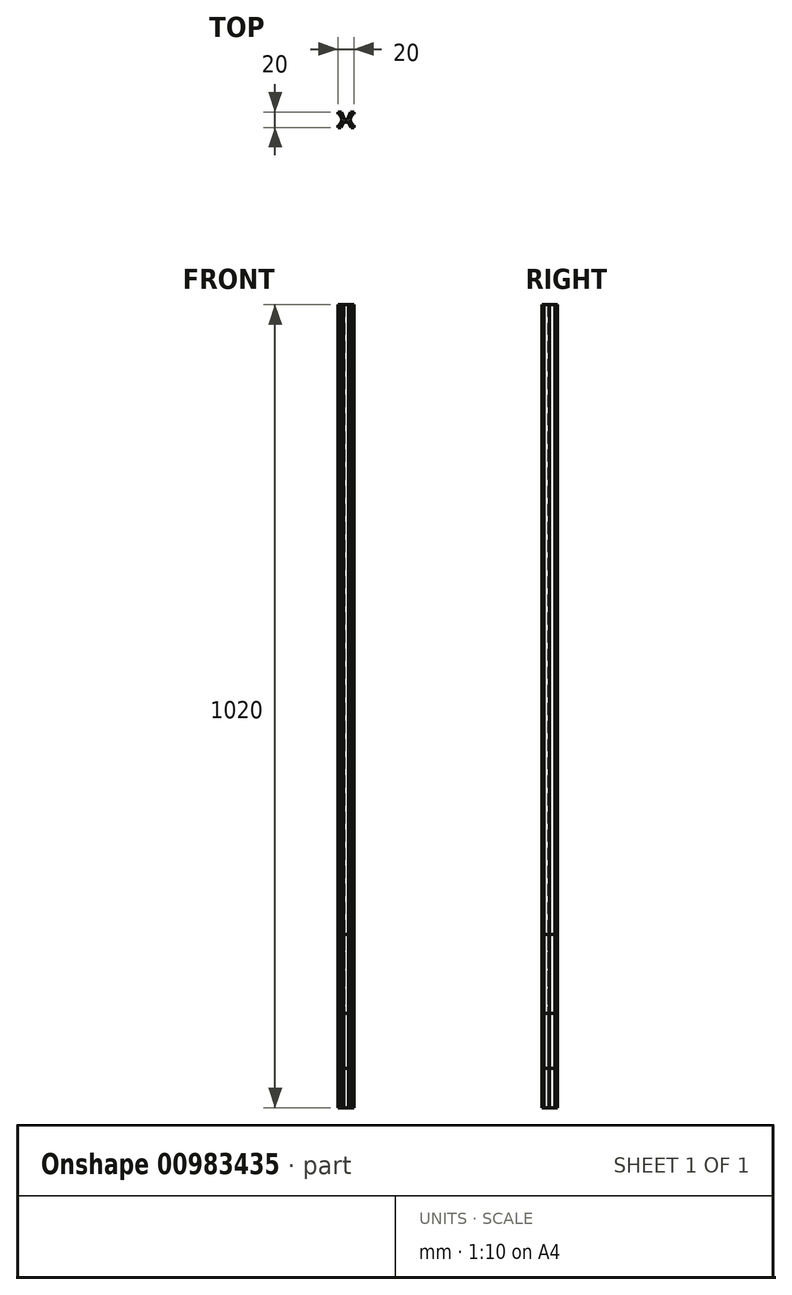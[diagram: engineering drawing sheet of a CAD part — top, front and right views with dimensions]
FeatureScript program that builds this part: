
annotation { "Feature Type Name" : "Feature", "Feature Type Description" : "" }
export const myFeature = defineFeature(function(context is Context, id is Id, definition is map)
    precondition{}
    {
        {
            var Q0;
            Q0=qCreatedBy(makeId("Top.planeOp"),FACE);
            var sketch = newSketch(context, id + "F0", { "sketchPlane" : qUnion([Q0])});
            skLineSegment(sketch, "E0", {"start": v(-10, 10) * mm, "end": v(-6, 10) * mm});
            skLineSegment(sketch, "E1", {"start": v(-6, 10) * mm, "end": v(-2, 0) * mm});
            skLineSegment(sketch, "E2", {"start": v(-2, 0) * mm, "end": v(2, 0) * mm});
            skLineSegment(sketch, "E3", {"start": v(2, 0) * mm, "end": v(6, 10) * mm});
            skLineSegment(sketch, "E4", {"start": v(6, 10) * mm, "end": v(10, 10) * mm});
            skLineSegment(sketch, "E5", {"start": v(10, 10) * mm, "end": v(10, 7) * mm});
            skLineSegment(sketch, "E6", {"start": v(7.8, 7) * mm, "end": v(10, 7) * mm});
            skLineSegment(sketch, "E7", {"start": v(7.8, 7) * mm, "end": v(5, 0) * mm});
            skLineSegment(sketch, "E8", {"start": v(5, 0) * mm, "end": v(7.8, -7) * mm});
            skLineSegment(sketch, "E9", {"start": v(7.8, -7) * mm, "end": v(10, -7) * mm});
            skLineSegment(sketch, "E10", {"start": v(10, -7) * mm, "end": v(10, -10) * mm});
            skLineSegment(sketch, "E11", {"start": v(6.28, -10) * mm, "end": v(10, -10) * mm});
            skLineSegment(sketch, "E12", {"start": v(6.28, -10) * mm, "end": v(3.48, -3) * mm});
            skLineSegment(sketch, "E13", {"start": v(3.48, -3) * mm, "end": v(-3.48, -3) * mm});
            skLineSegment(sketch, "E14", {"start": v(-3.48, -3) * mm, "end": v(-6.28, -10) * mm});
            skLineSegment(sketch, "E15", {"start": v(-6.28, -10) * mm, "end": v(-10, -10) * mm});
            skLineSegment(sketch, "E16", {"start": v(-10, -10) * mm, "end": v(-10, -7) * mm});
            skLineSegment(sketch, "E17", {"start": v(-10, -7) * mm, "end": v(-7.8, -7) * mm});
            skLineSegment(sketch, "E18", {"start": v(-7.8, -7) * mm, "end": v(-5, 0) * mm});
            skLineSegment(sketch, "E19", {"start": v(-5, 0) * mm, "end": v(-7.8, 7) * mm});
            skLineSegment(sketch, "E20", {"start": v(-7.8, 7) * mm, "end": v(-10, 7) * mm});
            skLineSegment(sketch, "E21", {"start": v(-10, 7) * mm, "end": v(-10, 10) * mm});
            skLineSegment(sketch, "E22", {"start": v(-6.28, -10) * mm, "end": v(6.28, -10) * mm, "construction": true});
            skLineSegment(sketch, "E23", {"start": v(-7.8, 7) * mm, "end": v(-4.8, 7) * mm, "construction": true});
            skLineSegment(sketch, "E24", {"start": v(-7.8, -7) * mm, "end": v(-5.08, -7) * mm, "construction": true});
            skSolve(sketch);
        }
        {
            var Q0;
            Q0=makeQuery(id+"F0.imprint","IMPRINT",FACE,{"disambiguationData":[TD([[makeQuery(id+"F0.imprint","IMPRINT",EDGE,{"derivedFrom":sQuery(id+"F0.wireOp",EDGE,"E0")}),-1.0]])]});
            extrude(context, id + "F1", {"entities" : qUnion([Q0]), "depth" : 50 * mm, "offsetDistance" : 25 * mm});
        }
        {
            var Q0;
            Q0 = qSketchRegion(id + "F0", true);
            extrude(context, id + "F2", {"entities" : qUnion([Q0]), "depth" : 1020 * mm, "offsetDistance" : 25 * mm});
        }
        {
            var Q0;
            Q0 = qSketchRegion(id + "F0", true);
            extrude(context, id + "F3", {"entities" : qUnion([Q0]), "depth" : 220 * mm, "offsetDistance" : 25 * mm});
        }
        {
            var Q0;
            Q0 = qSketchRegion(id + "F0", true);
            extrude(context, id + "F4", {"entities" : qUnion([Q0]), "depth" : 120 * mm, "offsetDistance" : 25 * mm});
        }
    });
